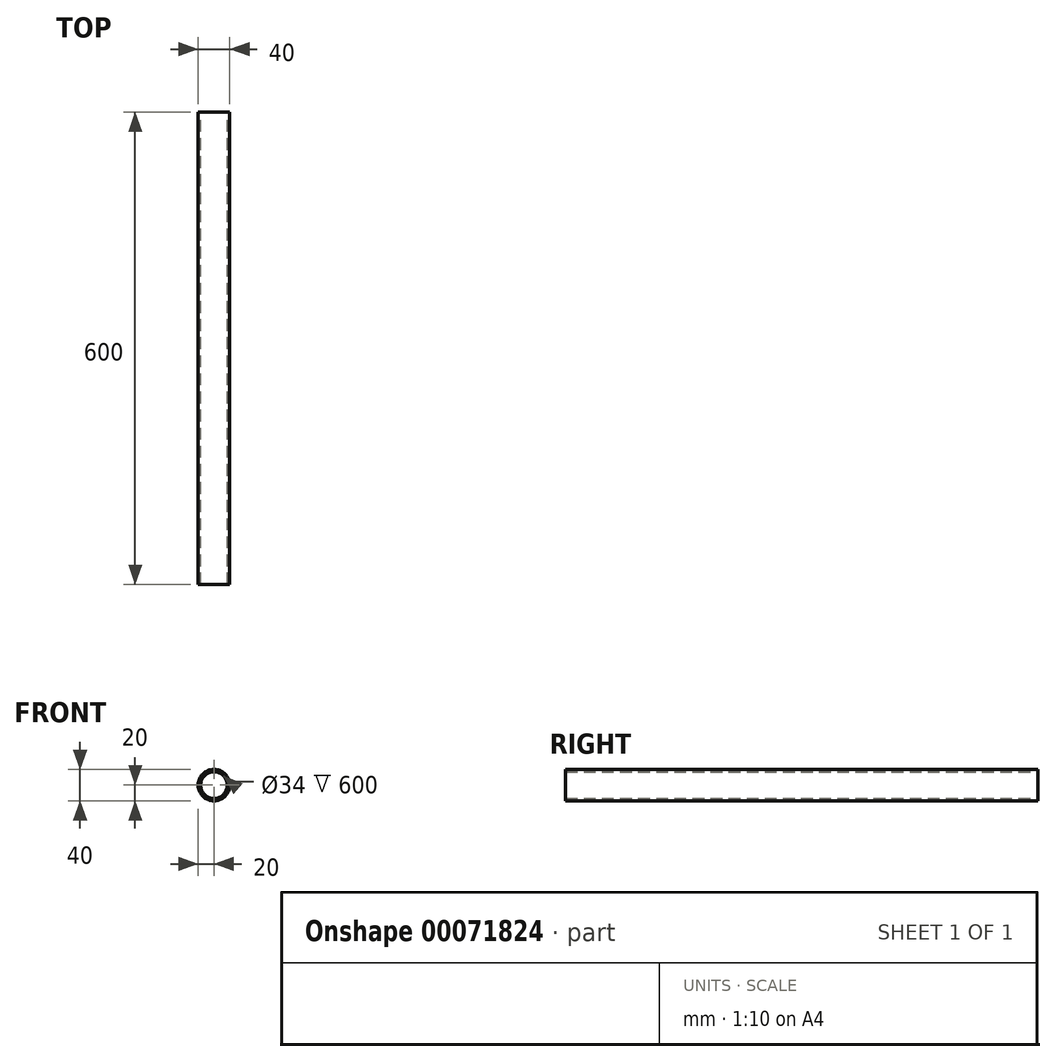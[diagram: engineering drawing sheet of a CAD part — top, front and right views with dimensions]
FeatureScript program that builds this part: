
annotation { "Feature Type Name" : "Feature", "Feature Type Description" : "" }
export const myFeature = defineFeature(function(context is Context, id is Id, definition is map)
    precondition{}
    {
        {
            var Q0;
            Q0=qCreatedBy(makeId("Front.planeOp"),FACE);
            var sketch = newSketch(context, id + "F0", { "sketchPlane" : qUnion([Q0])});
            skCircle(sketch, "E0", {"center": v(0, 0) * mm, "radius": 20 * mm});
            skCircle(sketch, "E1", {"center": v(0, 0) * mm, "radius": 17 * mm});
            skSolve(sketch);
        }
        {
            var Q0;
            Q0=makeQuery(id+"F0.imprint","IMPRINT",FACE,{"disambiguationData":[TD([[makeQuery(id+"F0.imprint","IMPRINT",EDGE,{"derivedFrom":sQuery(id+"F0.wireOp",EDGE,"E0")}),1.0]])]});
            extrude(context, id + "F1", {"entities" : qUnion([Q0]), "depth" : 600 * mm});
        }
    });
